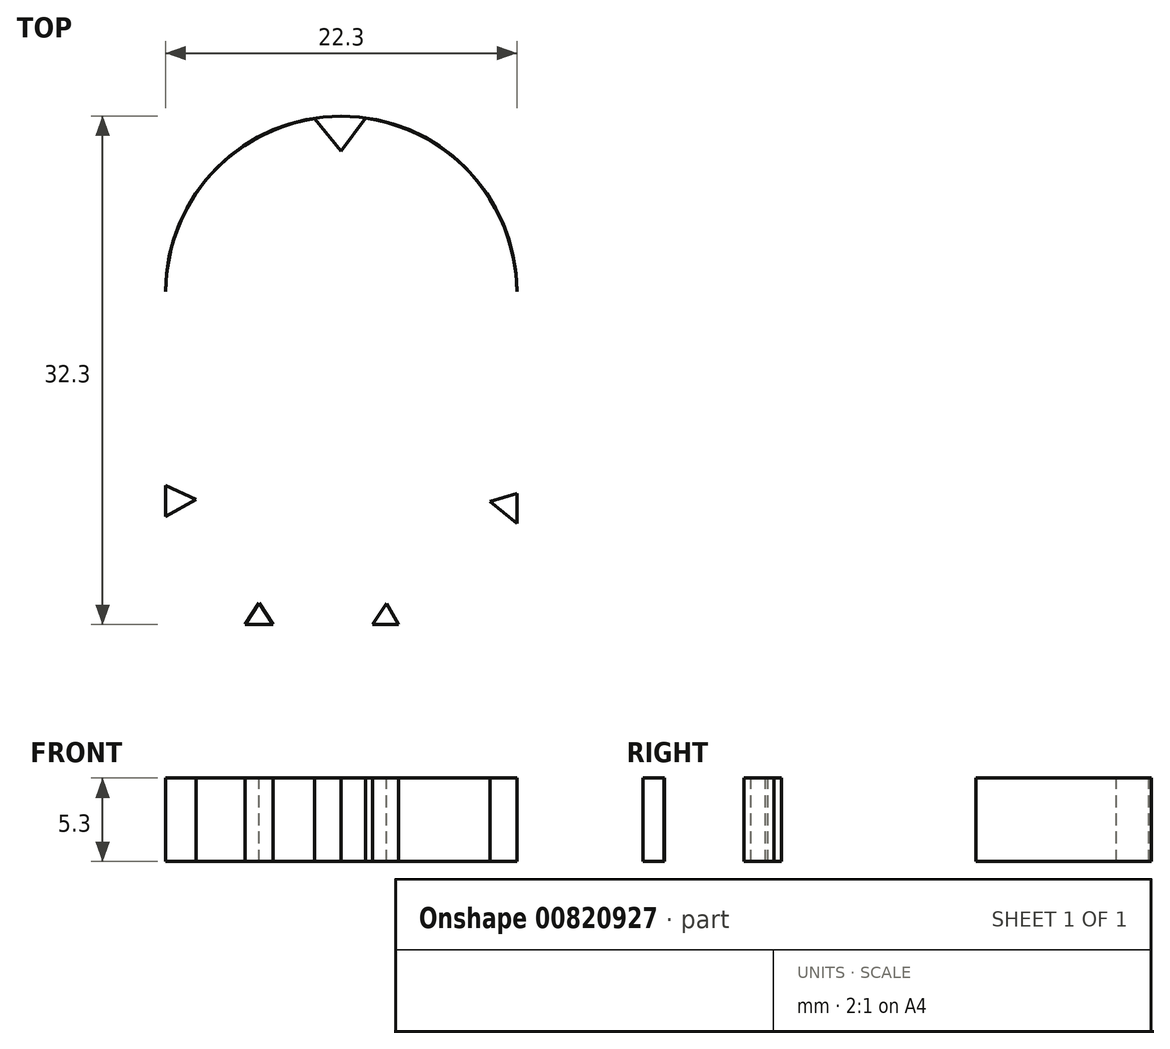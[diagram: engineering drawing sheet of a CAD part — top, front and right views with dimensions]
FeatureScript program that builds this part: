
annotation { "Feature Type Name" : "Feature", "Feature Type Description" : "" }
export const myFeature = defineFeature(function(context is Context, id is Id, definition is map)
    precondition{}
    {
        {
            var Q0;
            Q0=qCreatedBy(makeId("Top.planeOp"),FACE);
            var sketch = newSketch(context, id + "F0", { "sketchPlane" : qUnion([Q0])});
            skLineSegment(sketch, "E0.bottom", {"start": v(-8.15, -16.15) * mm, "end": v(8.15, -16.15) * mm});
            skLineSegment(sketch, "E0.top", {"start": v(0, 16.15) * mm, "end": v(0, 16.15) * mm});
            skLineSegment(sketch, "E0.left", {"start": v(-11.15, -13.15) * mm, "end": v(-11.15, 5) * mm});
            skLineSegment(sketch, "E0.right", {"start": v(11.15, -13.15) * mm, "end": v(11.15, 5) * mm});
            skPoint(sketch, "E0.middle", {"position": v(0, 0) * mm});
            skPoint(sketch, "E1.visualSharp", {"position": v(-11.15, 16.15) * mm});
            skArc(sketch, "E1.filletArc", {"start": v(0, 16.15) * mm, "mid": v(-7.88, 12.88) * mm, "end": v(-11.15, 5) * mm});
            skPoint(sketch, "E2.visualSharp", {"position": v(11.15, 16.15) * mm});
            skArc(sketch, "E2.filletArc", {"start": v(11.15, 5) * mm, "mid": v(7.88, 12.88) * mm, "end": v(0, 16.15) * mm});
            skPoint(sketch, "E3.visualSharp", {"position": v(-11.15, -16.15) * mm});
            skArc(sketch, "E3.filletArc", {"start": v(-11.15, -13.15) * mm, "mid": v(-10.27, -15.27) * mm, "end": v(-8.15, -16.15) * mm});
            skPoint(sketch, "E4.visualSharp", {"position": v(11.15, -16.15) * mm});
            skArc(sketch, "E4.filletArc", {"start": v(8.15, -16.15) * mm, "mid": v(10.27, -15.27) * mm, "end": v(11.15, -13.15) * mm});
            skSolve(sketch);
        }
        {
            var Q0;
            Q0=makeQuery(id+"F0.imprint","IMPRINT",FACE,{"disambiguationData":[TD([[makeQuery(id+"F0.imprint","IMPRINT",EDGE,{"derivedFrom":sQuery(id+"F0.wireOp",EDGE,"E0.bottom")}),1.0]])]});
            var sketch = newSketch(context, id + "F1", { "sketchPlane" : qUnion([Q0])});
            skLineSegment(sketch, "E5.bottom", {"start": v(0, 16.12) * mm, "end": v(0, 16.12) * mm});
            skLineSegment(sketch, "E5.top", {"start": v(-8.15, -16.18) * mm, "end": v(8.15, -16.18) * mm, "construction": true});
            skLineSegment(sketch, "E5.left", {"start": v(-11.15, 4.97) * mm, "end": v(-11.15, -13.18) * mm});
            skLineSegment(sketch, "E5.right", {"start": v(11.15, 4.97) * mm, "end": v(11.15, -13.18) * mm});
            skPoint(sketch, "E6.visualSharp", {"position": v(-11.15, -16.18) * mm});
            skArc(sketch, "E6.filletArc", {"start": v(-11.15, -13.18) * mm, "mid": v(-10.27, -15.3) * mm, "end": v(-8.15, -16.18) * mm});
            skPoint(sketch, "E7.visualSharp", {"position": v(11.15, -16.18) * mm});
            skArc(sketch, "E7.filletArc", {"start": v(8.15, -16.18) * mm, "mid": v(10.27, -15.3) * mm, "end": v(11.15, -13.18) * mm});
            skPoint(sketch, "E8.visualSharp", {"position": v(-11.15, 16.12) * mm});
            skArc(sketch, "E8.filletArc", {"start": v(0, 16.12) * mm, "mid": v(-7.88, 12.85) * mm, "end": v(-11.15, 4.97) * mm});
            skPoint(sketch, "E9.visualSharp", {"position": v(11.15, 16.12) * mm});
            skArc(sketch, "E9.filletArc", {"start": v(11.15, 4.97) * mm, "mid": v(7.88, 12.85) * mm, "end": v(0, 16.12) * mm});
            skLineSegment(sketch, "E10", {"start": v(-11.15, -7.33) * mm, "end": v(-9.21, -8.2) * mm});
            skLineSegment(sketch, "E11", {"start": v(-9.21, -8.2) * mm, "end": v(-11.15, -9.27) * mm});
            skLineSegment(sketch, "E12", {"start": v(-6.12, -16.18) * mm, "end": v(-5.2, -14.77) * mm});
            skLineSegment(sketch, "E13", {"start": v(11.15, -9.73) * mm, "end": v(9.46, -8.35) * mm});
            skLineSegment(sketch, "E14", {"start": v(9.46, -8.35) * mm, "end": v(11.15, -7.83) * mm});
            skLineSegment(sketch, "E15", {"start": v(1.95, -16.18) * mm, "end": v(2.86, -14.8) * mm});
            skLineSegment(sketch, "E16", {"start": v(2.86, -14.8) * mm, "end": v(3.64, -16.18) * mm});
            skLineSegment(sketch, "E17", {"start": v(-5.2, -14.77) * mm, "end": v(-4.3, -16.18) * mm});
            skLineSegment(sketch, "E18", {"start": v(-1.7, 15.99) * mm, "end": v(0, 13.92) * mm});
            skLineSegment(sketch, "E19", {"start": v(0, 13.92) * mm, "end": v(1.55, 16) * mm});
            skSolve(sketch);
        }
        {
            var Q0;
            Q0 = qSketchRegion(id + "F0", true);
            extrude(context, id + "F2", {"entities" : qUnion([Q0]), "oppositeDirection" : true, "depth" : 5.3 * mm, "offsetDistance" : 25 * mm});
        }
        {
            var Q0;
            {var subQ5=sQuery(id+"F1.wireOp",EDGE,"E10");Q0=makeQuery(id+"F1.imprint","IMPRINT",FACE,{"disambiguationData":[TD([[makeQuery(id+"F1.imprint","IMPRINT",EDGE,{"derivedFrom":subQ5}),1.0]])]});}
            extrude(context, id + "F3", {"entities" : qUnion([Q0]), "operationType" : NewBodyOperationType.REMOVE, "oppositeDirection" : true, "depth" : 5.3 * mm, "offsetDistance" : 25 * mm});
        }
    });
